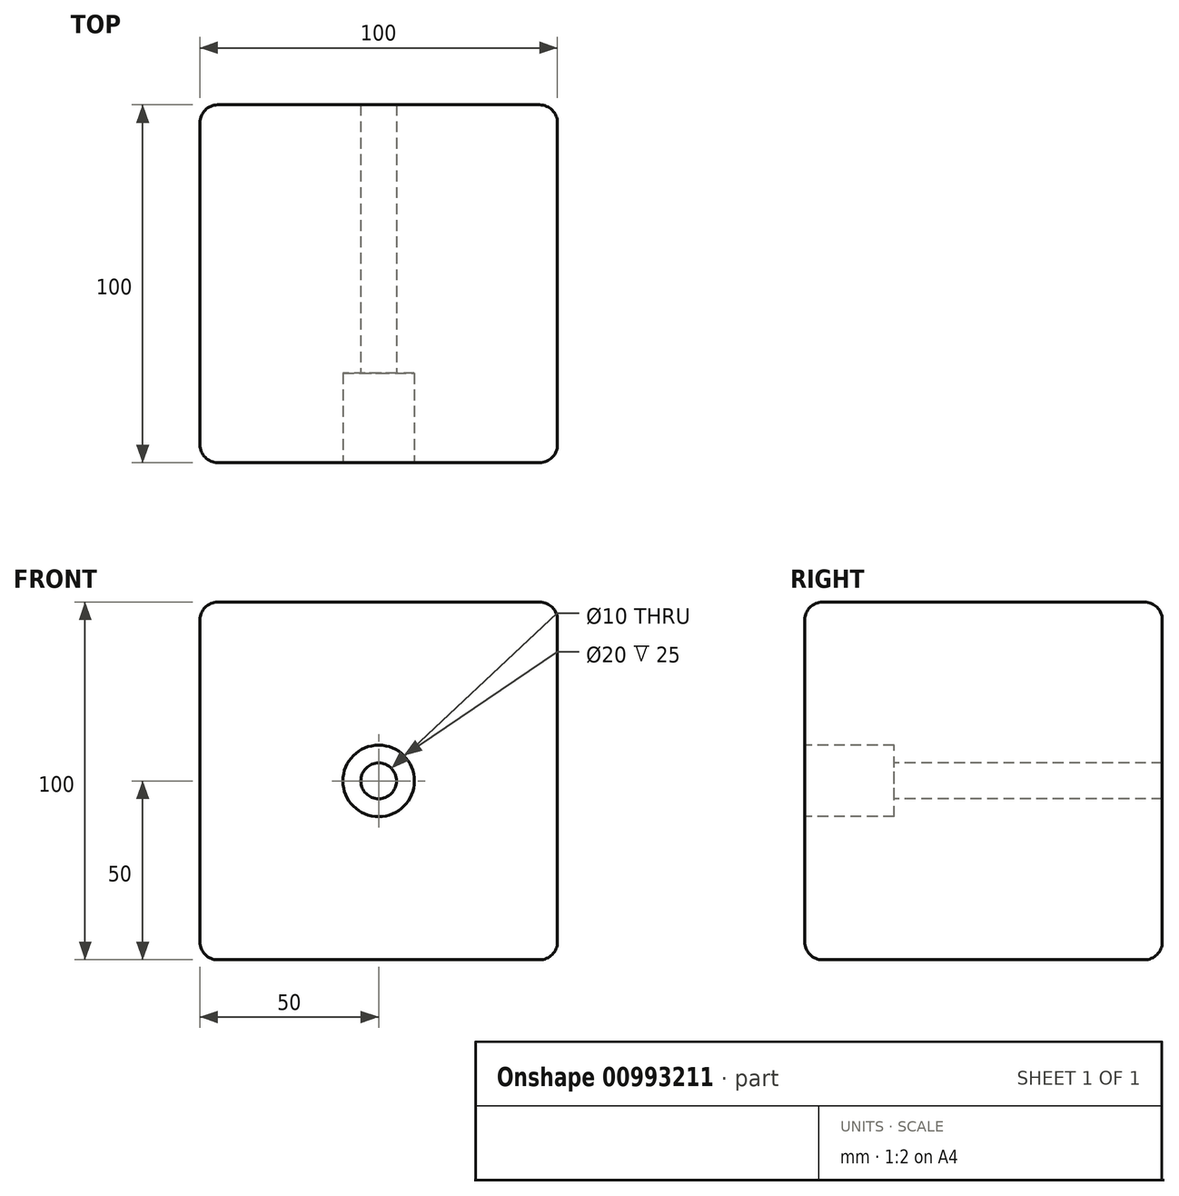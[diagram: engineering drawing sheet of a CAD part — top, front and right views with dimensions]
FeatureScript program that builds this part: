
annotation { "Feature Type Name" : "Feature", "Feature Type Description" : "" }
export const myFeature = defineFeature(function(context is Context, id is Id, definition is map)
    precondition{}
    {
        {
            var Q0;
            Q0=qCreatedBy(makeId("Front.planeOp"),FACE);
            var sketch = newSketch(context, id + "F0", { "sketchPlane" : qUnion([Q0])});
            skLineSegment(sketch, "E0.bottom", {"start": v(0, 0) * mm, "end": v(100, 0) * mm});
            skLineSegment(sketch, "E0.top", {"start": v(0, 100) * mm, "end": v(100, 100) * mm});
            skLineSegment(sketch, "E0.left", {"start": v(0, 0) * mm, "end": v(0, 100) * mm});
            skLineSegment(sketch, "E0.right", {"start": v(100, 0) * mm, "end": v(100, 100) * mm});
            skSolve(sketch);
        }
        {
            var Q0;
            Q0 = qSketchRegion(id + "F0", true);
            extrude(context, id + "F1", {"entities" : qUnion([Q0]), "depth" : 100 * mm, "offsetDistance" : 25 * mm});
        }
        {
            var Q0;
            Q0=makeQuery(id+"F1.opExtrude","CAP_FACE",FACE,{"disambiguationData":[OSD([sQuery(id+"F0.wireOp",EDGE,"E0.bottom"),sQuery(id+"F0.wireOp",EDGE,"E0.top"),sQuery(id+"F0.wireOp",EDGE,"E0.left"),sQuery(id+"F0.wireOp",EDGE,"E0.right")])],"isStart":false});
            var sketch = newSketch(context, id + "F2", { "sketchPlane" : qUnion([Q0])});
            skCircle(sketch, "E1", {"center": v(50, 50) * mm, "radius": 5 * mm});
            skSolve(sketch);
        }
        {
            var Q0;
            Q0 = qSketchRegion(id + "F2", true);
            extrude(context, id + "F3", {"entities" : qUnion([Q0]), "operationType" : NewBodyOperationType.REMOVE, "oppositeDirection" : true, "depth" : 100 * mm, "offsetDistance" : 25 * mm});
        }
        {
            var Q0;
            Q0=qCreatedBy(makeId("Front.planeOp"),FACE);
            cPlane(context, id + "F4", {"entities" : qUnion([Q0]), "cplaneType" : CPlaneType.OFFSET, "offset" : 50 * mm, "width" : 150 * mm, "height" : 150 * mm});
        }
        {
            var Q0;
            Q0=makeQuery(id+"F1.opExtrude","CAP_FACE",FACE,{"disambiguationData":[OSD([sQuery(id+"F0.wireOp",EDGE,"E0.bottom"),sQuery(id+"F0.wireOp",EDGE,"E0.top"),sQuery(id+"F0.wireOp",EDGE,"E0.left"),sQuery(id+"F0.wireOp",EDGE,"E0.right")])],"isStart":false});
            var sketch = newSketch(context, id + "F5", { "sketchPlane" : qUnion([Q0])});
            skCircle(sketch, "E2", {"center": v(50, 50) * mm, "radius": 10 * mm});
            skSolve(sketch);
        }
        {
            var Q0;
            Q0 = qSketchRegion(id + "F5", true);
            extrude(context, id + "F6", {"entities" : qUnion([Q0]), "operationType" : NewBodyOperationType.REMOVE, "oppositeDirection" : true, "depth" : 25 * mm, "offsetDistance" : 25 * mm});
        }
        {
            var Q0;
            Q0=makeQuery(id+"F1.opExtrude","SWEPT_EDGE",EDGE,{"disambiguationData":[OSD([sQuery(id+"F0.wireOp",EDGE,"E0.top"),sQuery(id+"F0.wireOp",EDGE,"E0.left")])]});
            var Q1;
            Q1=makeQuery(id+"F1.opExtrude","CAP_EDGE",EDGE,{"disambiguationData":[OSD([sQuery(id+"F0.wireOp",EDGE,"E0.top")])],"isStart":false});
            var Q2;
            Q2=makeQuery(id+"F1.opExtrude","SWEPT_EDGE",EDGE,{"disambiguationData":[OSD([sQuery(id+"F0.wireOp",EDGE,"E0.top"),sQuery(id+"F0.wireOp",EDGE,"E0.right")])]});
            var Q3;
            Q3=makeQuery(id+"F1.opExtrude","CAP_EDGE",EDGE,{"disambiguationData":[OSD([sQuery(id+"F0.wireOp",EDGE,"E0.top")])],"isStart":true});
            var Q4;
            Q4=makeQuery(id+"F1.opExtrude","CAP_EDGE",EDGE,{"disambiguationData":[OSD([sQuery(id+"F0.wireOp",EDGE,"E0.left")])],"isStart":false});
            var Q5;
            Q5=makeQuery(id+"F1.opExtrude","CAP_EDGE",EDGE,{"disambiguationData":[OSD([sQuery(id+"F0.wireOp",EDGE,"E0.bottom")])],"isStart":false});
            var Q6;
            Q6=makeQuery(id+"F1.opExtrude","CAP_EDGE",EDGE,{"disambiguationData":[OSD([sQuery(id+"F0.wireOp",EDGE,"E0.right")])],"isStart":false});
            var Q7;
            Q7=makeQuery(id+"F1.opExtrude","SWEPT_EDGE",EDGE,{"disambiguationData":[OSD([sQuery(id+"F0.wireOp",EDGE,"E0.bottom"),sQuery(id+"F0.wireOp",EDGE,"E0.right")])]});
            var Q8;
            Q8=makeQuery(id+"F1.opExtrude","CAP_EDGE",EDGE,{"disambiguationData":[OSD([sQuery(id+"F0.wireOp",EDGE,"E0.right")])],"isStart":true});
            var Q9;
            Q9=makeQuery(id+"F1.opExtrude","CAP_EDGE",EDGE,{"disambiguationData":[OSD([sQuery(id+"F0.wireOp",EDGE,"E0.bottom")])],"isStart":true});
            var Q10;
            Q10=makeQuery(id+"F1.opExtrude","CAP_EDGE",EDGE,{"disambiguationData":[OSD([sQuery(id+"F0.wireOp",EDGE,"E0.left")])],"isStart":true});
            var Q11;
            Q11=makeQuery(id+"F1.opExtrude","SWEPT_EDGE",EDGE,{"disambiguationData":[OSD([sQuery(id+"F0.wireOp",EDGE,"E0.bottom"),sQuery(id+"F0.wireOp",EDGE,"E0.left")])]});
            fillet(context, id + "F7", {"entities" : qUnion([Q0, Q1, Q2, Q3, Q4, Q5, Q6, Q7, Q8, Q9, Q10, Q11]), "radius" : 5 * mm, "tangentPropagation" : true, "allowEdgeOverflow" : false});
        }
    });
